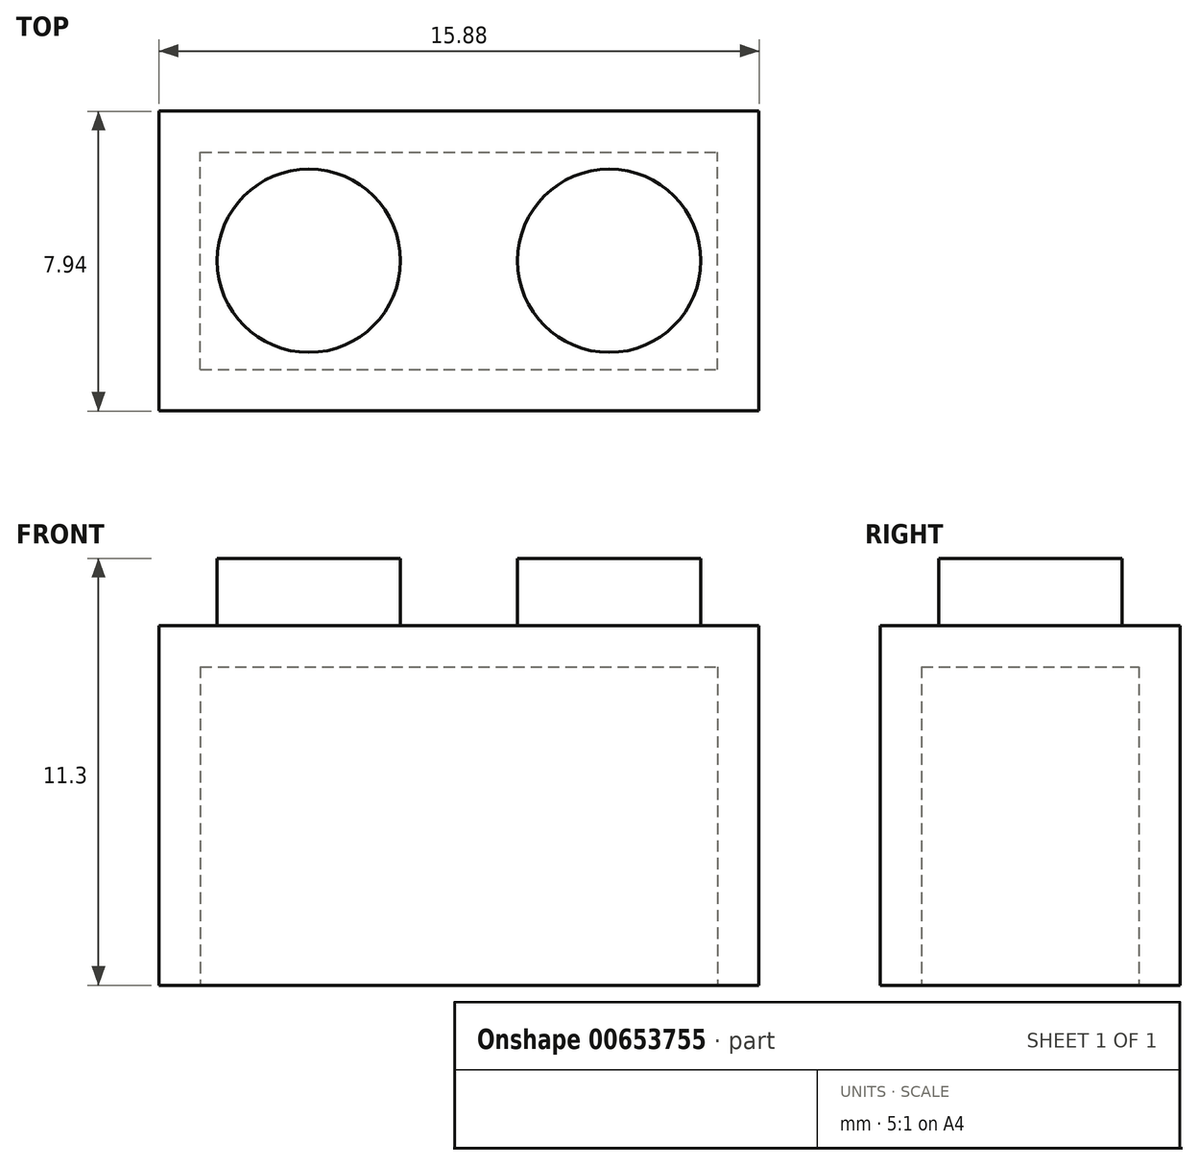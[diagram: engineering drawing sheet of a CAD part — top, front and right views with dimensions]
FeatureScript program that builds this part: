
annotation { "Feature Type Name" : "Feature", "Feature Type Description" : "" }
export const myFeature = defineFeature(function(context is Context, id is Id, definition is map)
    precondition{}
    {
        {
            var Q0;
            Q0=qCreatedBy(makeId("Top.planeOp"),FACE);
            var sketch = newSketch(context, id + "F0", { "sketchPlane" : qUnion([Q0])});
            skLineSegment(sketch, "E0.bottom", {"start": v(-28.9, 27.88) * mm, "end": v(-13.02, 27.88) * mm});
            skLineSegment(sketch, "E0.top", {"start": v(-28.9, 19.94) * mm, "end": v(-13.02, 19.94) * mm});
            skLineSegment(sketch, "E0.left", {"start": v(-28.9, 27.88) * mm, "end": v(-28.9, 19.94) * mm});
            skLineSegment(sketch, "E0.right", {"start": v(-13.02, 27.88) * mm, "end": v(-13.02, 19.94) * mm});
            skSolve(sketch);
        }
        {
            var Q0;
            Q0 = qSketchRegion(id + "F0", true);
            extrude(context, id + "F1", {"entities" : qUnion([Q0]), "depth" : 9.52 * mm, "offsetDistance" : 25.4 * mm});
        }
        {
            var Q0;
            Q0=makeQuery(id+"F1.opExtrude","CAP_FACE",FACE,{"disambiguationData":[OSD([sQuery(id+"F0.wireOp",EDGE,"E0.bottom"),sQuery(id+"F0.wireOp",EDGE,"E0.top"),sQuery(id+"F0.wireOp",EDGE,"E0.left"),sQuery(id+"F0.wireOp",EDGE,"E0.right")])],"isStart":false});
            var sketch = newSketch(context, id + "F2", { "sketchPlane" : qUnion([Q0])});
            skCircle(sketch, "E1", {"center": v(-24.94, 23.92) * mm, "radius": 2.43 * mm});
            skSolve(sketch);
        }
        {
            var Q0;
            Q0=makeQuery(id+"F2.imprint","IMPRINT",FACE,{"disambiguationData":[TD([[makeQuery(id+"F2.imprint","IMPRINT",EDGE,{"derivedFrom":sQuery(id+"F2.wireOp",EDGE,"E1")}),-1.0]])]});
            var sketch = newSketch(context, id + "F3", { "sketchPlane" : qUnion([Q0])});
            skCircle(sketch, "E2", {"center": v(-16.99, 23.92) * mm, "radius": 2.43 * mm});
            skSolve(sketch);
        }
        {
            var Q0;
            Q0 = qSketchRegion(id + "F2", true);
            extrude(context, id + "F4", {"entities" : qUnion([Q0]), "operationType" : NewBodyOperationType.ADD, "depth" : 1.78 * mm, "offsetDistance" : 25.4 * mm});
        }
        {
            var Q0;
            Q0 = qSketchRegion(id + "F3", true);
            extrude(context, id + "F5", {"entities" : qUnion([Q0]), "operationType" : NewBodyOperationType.ADD, "depth" : 1.78 * mm, "offsetDistance" : 25.4 * mm});
        }
        {
            var Q0;
            Q0=makeQuery(id+"F1.opExtrude","CAP_FACE",FACE,{"disambiguationData":[OSD([sQuery(id+"F0.wireOp",EDGE,"E0.bottom"),sQuery(id+"F0.wireOp",EDGE,"E0.top"),sQuery(id+"F0.wireOp",EDGE,"E0.left"),sQuery(id+"F0.wireOp",EDGE,"E0.right")])],"isStart":true});
            var sketch = newSketch(context, id + "F6", { "sketchPlane" : qUnion([Q0])});
            skLineSegment(sketch, "E3.bottom", {"start": v(-27.8, -21.04) * mm, "end": v(-14.12, -21.04) * mm});
            skLineSegment(sketch, "E3.top", {"start": v(-27.8, -26.79) * mm, "end": v(-14.12, -26.79) * mm});
            skLineSegment(sketch, "E3.left", {"start": v(-27.8, -21.04) * mm, "end": v(-27.8, -26.79) * mm});
            skLineSegment(sketch, "E3.right", {"start": v(-14.12, -21.04) * mm, "end": v(-14.12, -26.79) * mm});
            skSolve(sketch);
        }
        {
            var Q0;
            Q0 = qSketchRegion(id + "F6", true);
            extrude(context, id + "F7", {"entities" : qUnion([Q0]), "operationType" : NewBodyOperationType.REMOVE, "oppositeDirection" : true, "depth" : 8.43 * mm, "offsetDistance" : 25.4 * mm});
        }
    });
